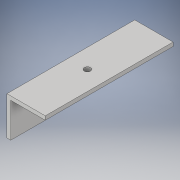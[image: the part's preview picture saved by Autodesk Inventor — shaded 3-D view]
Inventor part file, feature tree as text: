
AUTODESK INVENTOR PART (.ipt)
format: ipt  version: 2019 (Build 230136000, 136)  size: 102,912 bytes
history: native  units: mm
features: extrude x2, sketch x2
ambient origin geometry x8: Origin, YZ Plane, XZ Plane, XY Plane, X Axis, Y Axis, Z Axis, Center Point
bodies: Solid1 (feature_tree)
feature tree (4):
  extrude  "Extrusion1"  Depth=30.0mm
  extrude  "Extrusion2"  Depth=3.0mm
  sketch  "Sketch1"  dims[d0=30.0mm d1=30.0mm]
  sketch  "Sketch2"  dims[d2=27.0mm d3=3.0mm d4=100.0mm d5=0.0mm d6=15.0mm d7=100.0mm d8=0.0mm]
